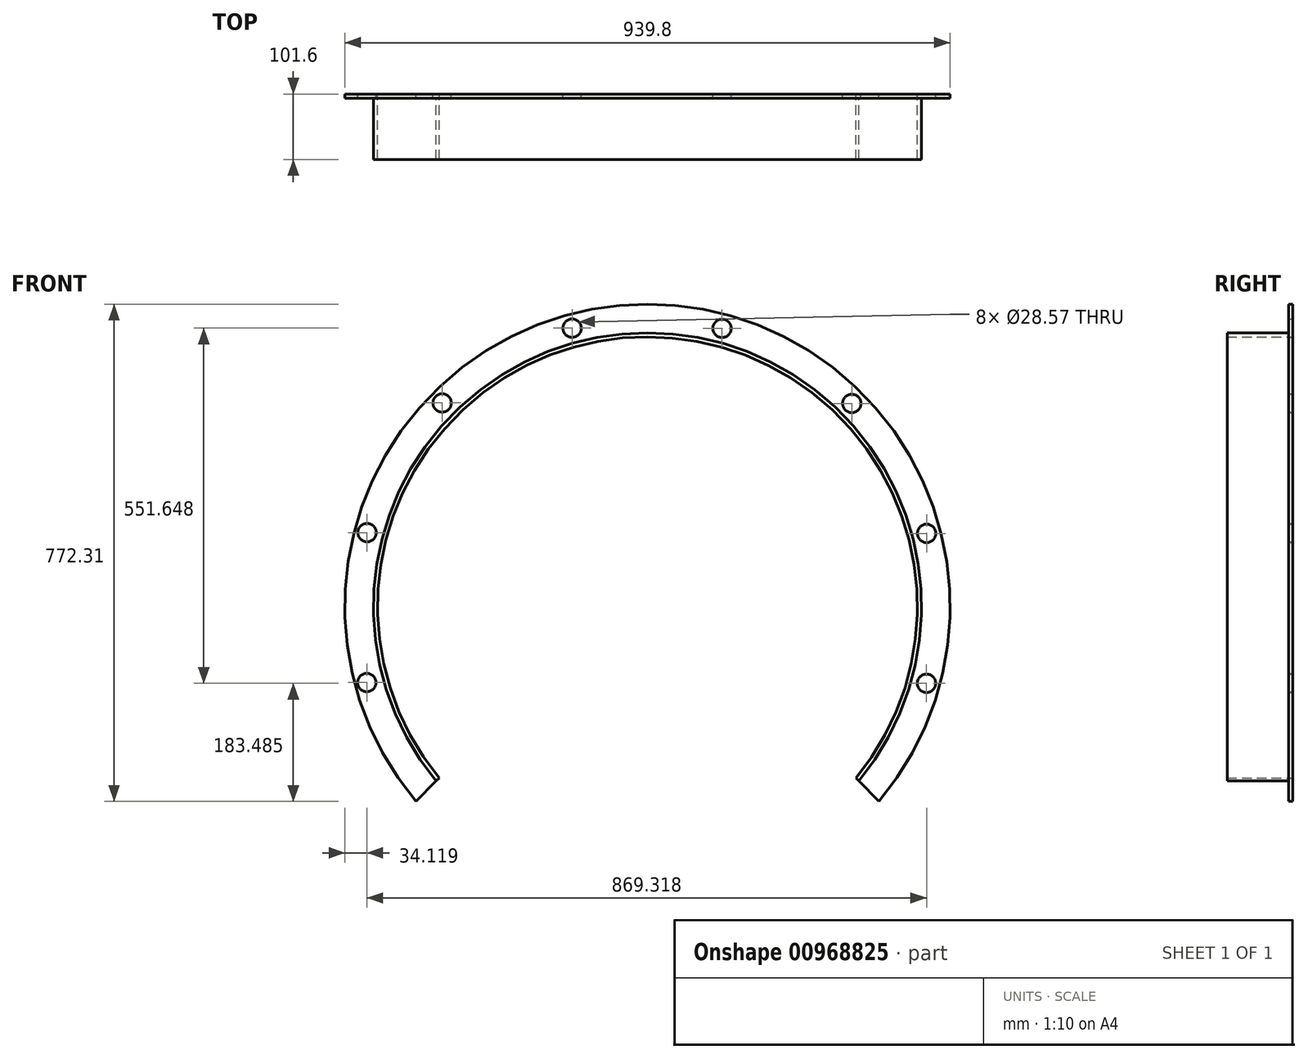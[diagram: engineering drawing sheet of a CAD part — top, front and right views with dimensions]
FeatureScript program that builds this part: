
annotation { "Feature Type Name" : "Feature", "Feature Type Description" : "" }
export const myFeature = defineFeature(function(context is Context, id is Id, definition is map)
    precondition{}
    {
        {
            var Q0;
            Q0=qCreatedBy(makeId("Front.planeOp"),FACE);
            var sketch = newSketch(context, id + "F0", { "sketchPlane" : qUnion([Q0])});
            skArc(sketch, "E0", {"start": v(359.66, -302.41) * mm, "mid": v(0, 469.9) * mm, "end": v(-359.66, -302.41) * mm});
            skLineSegment(sketch, "E1", {"start": v(0, 0) * mm, "end": v(0, 469.9) * mm, "construction": true});
            skLineSegment(sketch, "E2", {"start": v(0, 0) * mm, "end": v(121.62, 453.89) * mm, "construction": true});
            skPoint(sketch, "E3", {"position": v(115.87, 432.42) * mm});
            skCircle(sketch, "E4", {"center": v(115.87, 432.42) * mm, "radius": 14.29 * mm});
            skCircle(sketch, "E5.1.0", {"center": v(-116.99, 432.72) * mm, "radius": 14.29 * mm});
            skCircle(sketch, "E5.2.0", {"center": v(-318.8, 316.56) * mm, "radius": 14.29 * mm});
            skCircle(sketch, "E5.3.0", {"center": v(-435.48, 115.05) * mm, "radius": 14.29 * mm});
            skCircle(sketch, "E5.4.0", {"center": v(-435.78, -117.8) * mm, "radius": 14.29 * mm});
            skCircle(sketch, "E5.9.0", {"center": v(433.24, -118.93) * mm, "radius": 14.29 * mm});
            skCircle(sketch, "E5.10.0", {"center": v(433.54, 113.93) * mm, "radius": 14.29 * mm});
            skCircle(sketch, "E5.11.0", {"center": v(317.37, 315.73) * mm, "radius": 14.29 * mm});
            skPoint(sketch, "E5.center", {"position": v(-1.12, -1.94) * mm});
            skArc(sketch, "E6", {"start": v(345, -287.76) * mm, "mid": v(0, 449.26) * mm, "end": v(-345, -287.76) * mm, "construction": true});
            skArc(sketch, "E7", {"start": v(250.83, 0) * mm, "mid": v(0, 250.83) * mm, "end": v(-250.83, 0) * mm});
            skLineSegment(sketch, "E8", {"start": v(250.83, 0) * mm, "end": v(250.83, -151.48) * mm});
            skLineSegment(sketch, "E9", {"start": v(-250.83, 0) * mm, "end": v(-250.83, -151.48) * mm});
            skPoint(sketch, "E10", {"position": v(345, -287.76) * mm});
            skLineSegment(sketch, "E11", {"start": v(280.57, -223.31) * mm, "end": v(359.66, -302.41) * mm});
            skPoint(sketch, "E12.newPointA", {"position": v(250.83, -404.74) * mm});
            skPoint(sketch, "E12.newPointB", {"position": v(242.93, -185.66) * mm});
            skArc(sketch, "E12.filletArc", {"start": v(250.83, -151.48) * mm, "mid": v(258.56, -190.35) * mm, "end": v(280.57, -223.31) * mm});
            skArc(sketch, "E13.MirrorCS", {"start": v(-250.83, -151.48) * mm, "mid": v(-258.56, -190.35) * mm, "end": v(-280.57, -223.31) * mm});
            skLineSegment(sketch, "E14.MirrorCS", {"start": v(-280.57, -223.31) * mm, "end": v(-359.66, -302.41) * mm});
            skArc(sketch, "E15.trimOffspring", {"start": v(323.58, -266.33) * mm, "mid": v(0.13, 419.2) * mm, "end": v(-323.5, -266.25) * mm});
            skArc(sketch, "E16.trimOffspring", {"start": v(328.1, -270.84) * mm, "mid": v(0.13, 425.56) * mm, "end": v(-328, -270.76) * mm});
            skSolve(sketch);
        }
        {
            var Q0;
            {var subQ8=sQuery(id+"F0.wireOp",EDGE,"E0");Q0=makeQuery(id+"F0.imprint","IMPRINT",FACE,{"disambiguationData":[TD([[makeQuery(id+"F0.imprint","IMPRINT",EDGE,{"derivedFrom":subQ8}),1.0]])]});}
            extrude(context, id + "F1", {"entities" : qUnion([Q0]), "depth" : 6.35 * mm, "offsetDistance" : 25.4 * mm});
        }
        {
            var Q0;
            {var subQ0=sQuery(id+"F0.wireOp",EDGE,"E15.trimOffspring");Q0=makeQuery(id+"F0.imprint","IMPRINT",FACE,{"disambiguationData":[TD([[makeQuery(id+"F0.imprint","IMPRINT",EDGE,{"derivedFrom":subQ0}),-1.0]])]});}
            extrude(context, id + "F2", {"entities" : qUnion([Q0]), "operationType" : NewBodyOperationType.ADD, "depth" : 101.6 * mm, "offsetDistance" : 25.4 * mm});
        }
    });
